# Revit family: Lighting_Linear_LED_StarTek_Perimeter-Slim-Beam1
name_source: partatom
category: Lighting Fixtures
units: mm (PartAtom-declared; Revit-internal decimal feet)

## family parameters
Cut with Voids When Loaded = No
Host = Face
Light Source = Yes
OmniClass Number = 23.80.70.11
OmniClass Title = Luminaries for Internal Lighting
Part Type = Normal
Room Calculation Point = No
Round Connector Dimension = Use Diameter
Shared = No

## types (1)
- Default - please load Revit Family Type Catalog
    Apparent Load = 13 VA
    Assembly Code = D5020200
    CRI = 80
    Color Filter = 16777215
    Default Elevation = 48 "
    Description = Perimeter Slim Beam
    Dimming Lamp Color Temperature Shift = <None>
    Distribution = SD-SatinIce Diffused
    Emit Shape Visible in Rendering = No
    Emit from Rectangle Width = 2 "
    Frequency = 60 Hz
    Height = 3.5 "
    Input Wattage = 12 W
    Keynote = 16500
    Lamp = LED
    Length = 48 "
    Manufacturer = StarTek Lighting
    Model = PSLIM
    Number of Poles = 1
    Phase = 1
    Photometric Note = Import IES files https://starteklightingamerica.com
    Photometric Web File = Generic Light Source Shown : Please download and link the IES file that best matches your fixture specification
    Power Factor = 0.93
    Product data url = https://bimobject.com
    Tilt Angle = 90.00°
    URL = https://starteklightingamerica.com
    Voltage = 347 V
    Voltage Range = 347V
    Wattage Comments = Efficacy up to 116 lm/W
    Weight = 0.00 lbf
    Width = 2.1 "
    Z_DR = Mounting : Trimless Drywall (DR)
    Z_DWCB = Mounting : Drywall with Cosmetic Bezzle (DWCB)
    Z_DWSF = Mounting : Drywall with Spackle Flange (DWSF)
    Z_Option End = Straight Run : End Fixture
    Z_Option Middle = Straight Run : Middle Fixture
    Z_Option Standalone = Straight Run : Standalone Fixture
    Z_Option Start = Straight Run : Start Fixture
    Z_STB1 = Mounting : 9/16" Screw Slotted T-BAR (STB1)
    Z_TB1 = Mounting : 9/16" T-BAR (TB1)
    Z_TB2 = Mounting : 15/16" T-BAR (TB2)
    Z_TBT1 = Mounting : 9/16" T-BAR Tegular (TBT1)
    Z_TBT2 = Mounting : 15/16" T-BAR Tegular (TBT2)

## geometry (parser evidence)
native form markers: Sweep x12
no freeform markers — native parametric forms only
